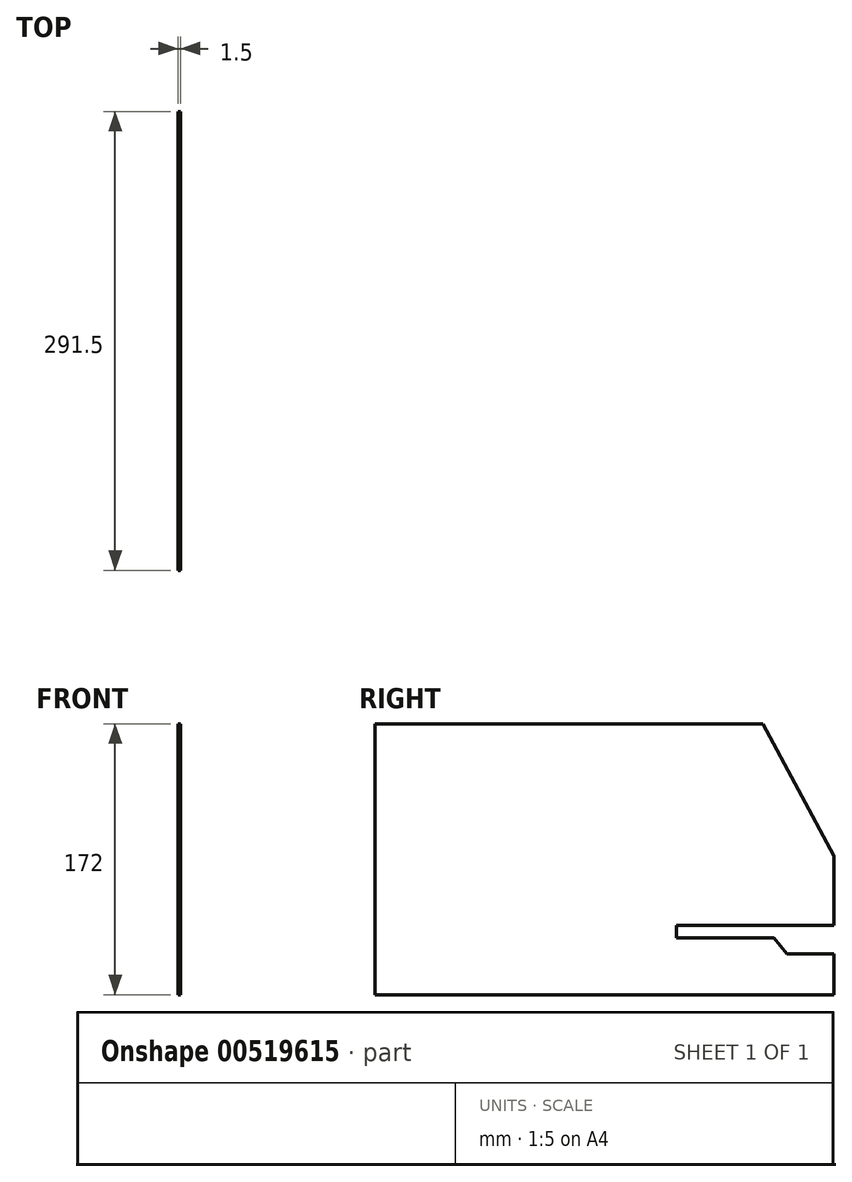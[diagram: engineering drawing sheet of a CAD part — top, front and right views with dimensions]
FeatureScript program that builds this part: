
annotation { "Feature Type Name" : "Feature", "Feature Type Description" : "" }
export const myFeature = defineFeature(function(context is Context, id is Id, definition is map)
    precondition{}
    {
        {
            var Q0;
            Q0=qCreatedBy(makeId("Right.planeOp"),FACE);
            var sketch = newSketch(context, id + "F0", { "sketchPlane" : qUnion([Q0])});
            skLineSegment(sketch, "E0.bottom", {"start": v(101.5, 86) * mm, "end": v(-145, 86) * mm});
            skLineSegment(sketch, "E0.top", {"start": v(146.5, -86) * mm, "end": v(-145, -86) * mm});
            skLineSegment(sketch, "E0.left", {"start": v(146.5, 2) * mm, "end": v(146.5, -42) * mm});
            skLineSegment(sketch, "E0.right", {"start": v(-145, 86) * mm, "end": v(-145, -86) * mm});
            skPoint(sketch, "E0.middle", {"position": v(0.75, 0) * mm});
            skLineSegment(sketch, "E1", {"start": v(101.5, 86) * mm, "end": v(146.5, 2) * mm});
            skLineSegment(sketch, "E2", {"start": v(146.5, -42) * mm, "end": v(46.5, -42) * mm});
            skLineSegment(sketch, "E3", {"start": v(46.5, -42) * mm, "end": v(46.5, -50) * mm});
            skLineSegment(sketch, "E4", {"start": v(46.5, -50) * mm, "end": v(108.5, -50) * mm});
            skLineSegment(sketch, "E5", {"start": v(108.5, -50) * mm, "end": v(116.5, -60) * mm});
            skLineSegment(sketch, "E6", {"start": v(116.5, -60) * mm, "end": v(146.5, -60) * mm});
            skLineSegment(sketch, "E7.trimOffspring", {"start": v(146.5, -60) * mm, "end": v(146.5, -86) * mm});
            skSolve(sketch);
        }
        {
            var Q0;
            Q0 = qSketchRegion(id + "F0", true);
            extrude(context, id + "F1", {"entities" : qUnion([Q0]), "depth" : 1.5 * mm, "offsetDistance" : 25 * mm});
        }
    });
